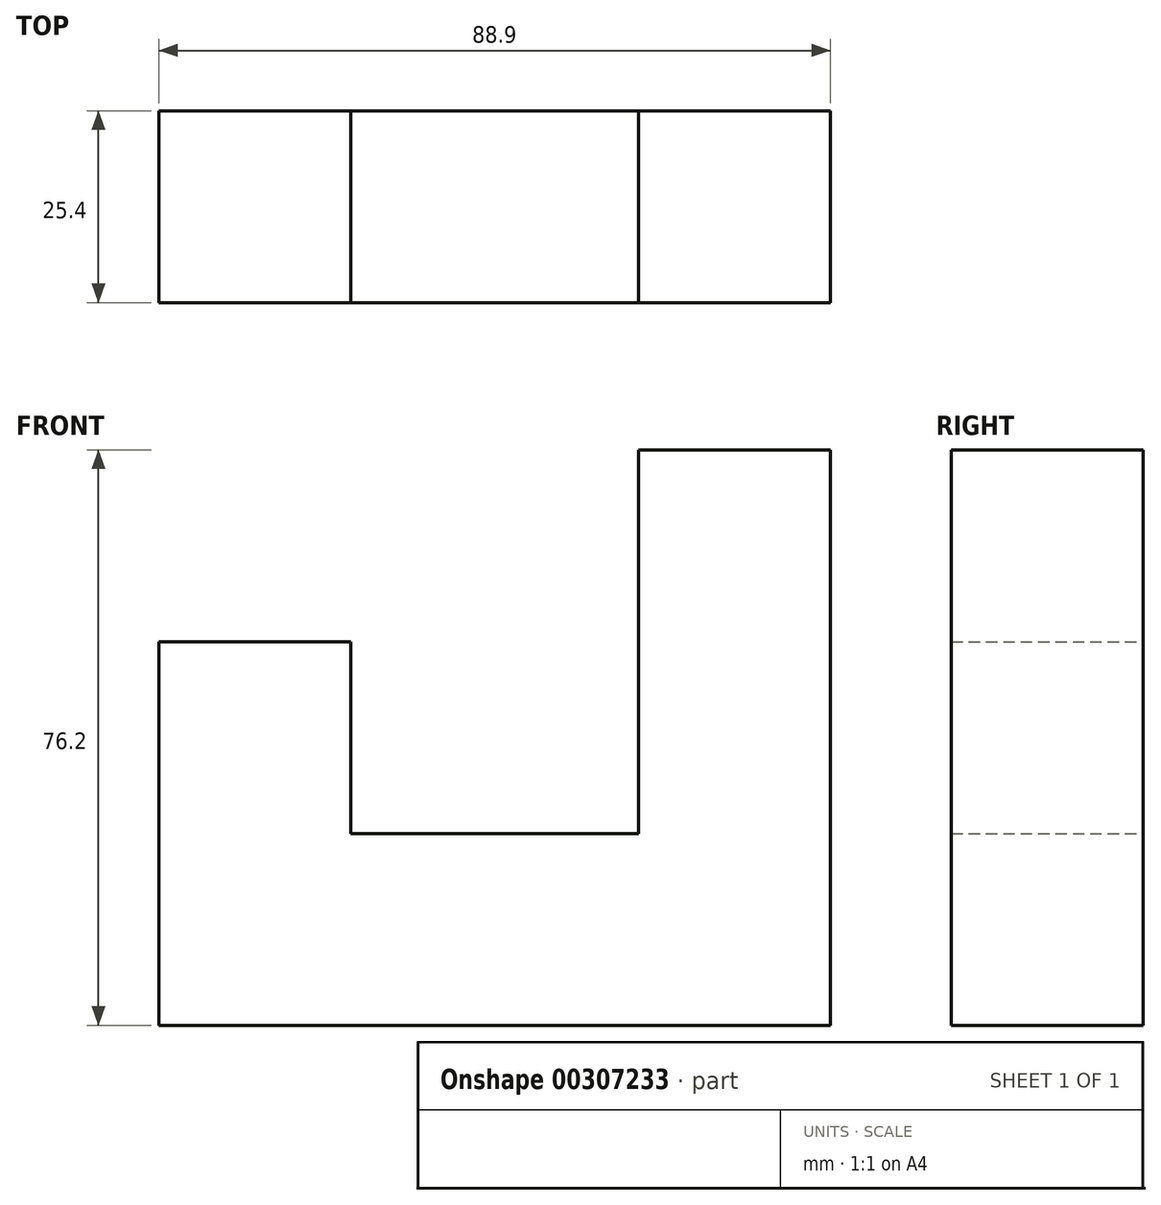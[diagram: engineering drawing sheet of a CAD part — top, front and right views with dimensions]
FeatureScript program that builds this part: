
annotation { "Feature Type Name" : "Feature", "Feature Type Description" : "" }
export const myFeature = defineFeature(function(context is Context, id is Id, definition is map)
    precondition{}
    {
        {
            var Q0;
            Q0=qCreatedBy(makeId("Front.planeOp"),FACE);
            var sketch = newSketch(context, id + "F0", { "sketchPlane" : qUnion([Q0])});
            skLineSegment(sketch, "E0", {"start": v(32.16, -41.88) * mm, "end": v(32.16, 34.32) * mm});
            skLineSegment(sketch, "E1", {"start": v(32.16, 34.32) * mm, "end": v(6.76, 34.32) * mm});
            skLineSegment(sketch, "E2", {"start": v(6.76, 34.32) * mm, "end": v(6.76, -16.48) * mm});
            skLineSegment(sketch, "E3", {"start": v(6.76, -16.48) * mm, "end": v(-31.34, -16.48) * mm});
            skLineSegment(sketch, "E4", {"start": v(-31.34, -16.48) * mm, "end": v(-31.34, 8.92) * mm});
            skLineSegment(sketch, "E5", {"start": v(-31.34, 8.92) * mm, "end": v(-56.74, 8.92) * mm});
            skLineSegment(sketch, "E6", {"start": v(-56.74, 8.92) * mm, "end": v(-56.74, -41.88) * mm});
            skLineSegment(sketch, "E7", {"start": v(-56.74, -41.88) * mm, "end": v(32.16, -41.88) * mm});
            skSolve(sketch);
        }
        {
            var Q0;
            Q0=makeQuery(id+"F0.imprint","IMPRINT",FACE,{"disambiguationData":[TD([[makeQuery(id+"F0.imprint","IMPRINT",EDGE,{"derivedFrom":sQuery(id+"F0.wireOp",EDGE,"E0")}),1.0]])]});
            extrude(context, id + "F1", {"entities" : qUnion([Q0]), "depth" : 25.4 * mm});
        }
    });
